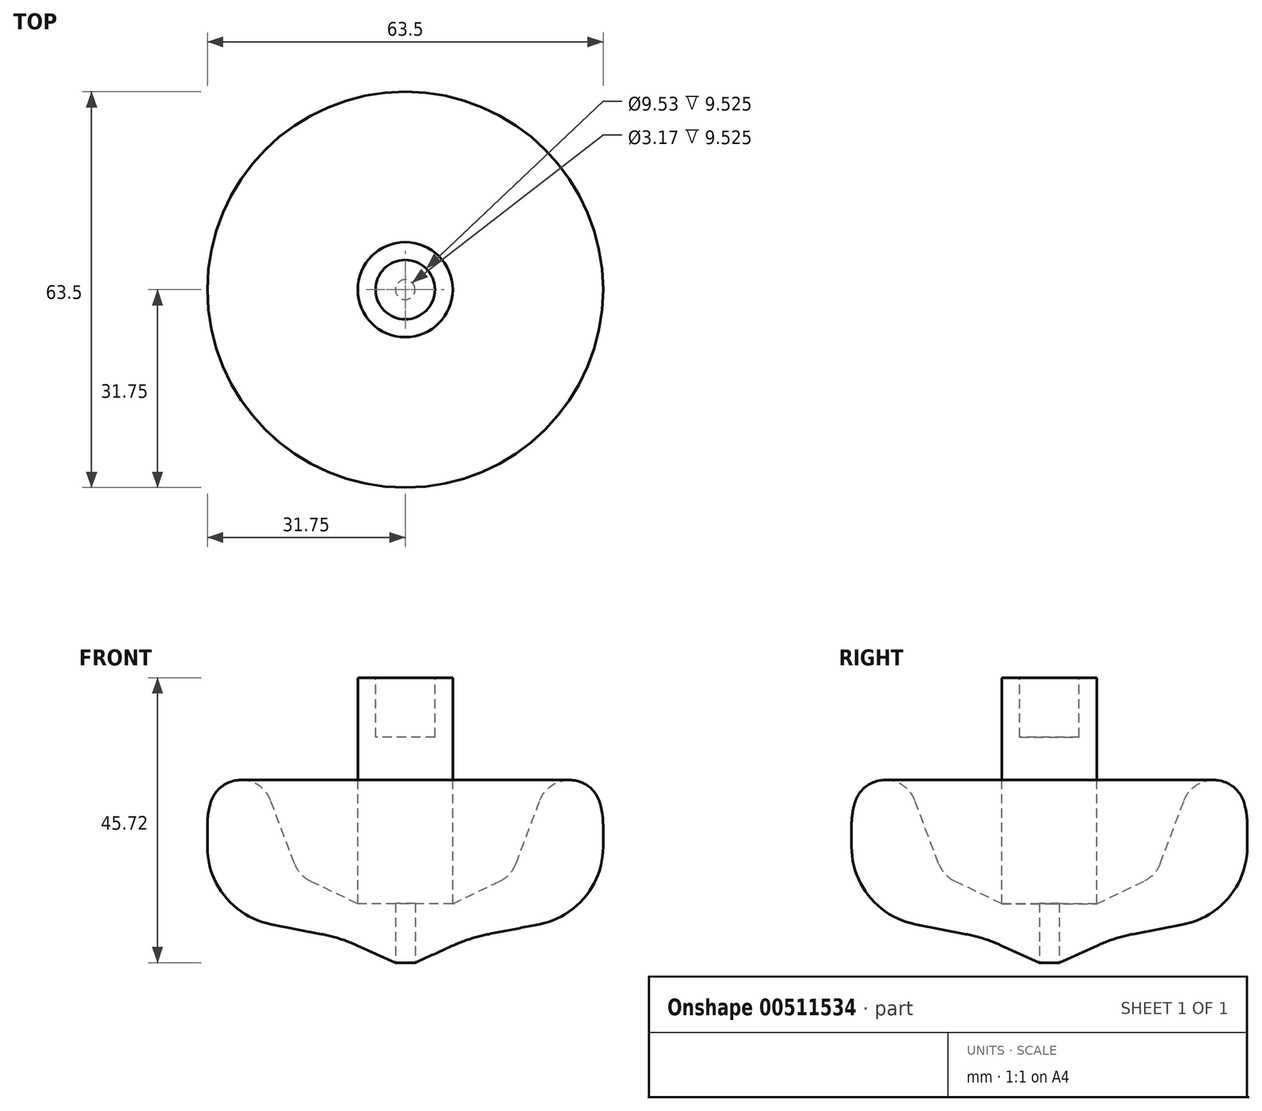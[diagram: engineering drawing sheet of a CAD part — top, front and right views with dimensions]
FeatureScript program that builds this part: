
annotation { "Feature Type Name" : "Feature", "Feature Type Description" : "" }
export const myFeature = defineFeature(function(context is Context, id is Id, definition is map)
    precondition{}
    {
        {
            var Q0;
            Q0=qCreatedBy(makeId("Front.planeOp"),FACE);
            var sketch = newSketch(context, id + "F0", { "sketchPlane" : qUnion([Q0])});
            skLineSegment(sketch, "E0", {"start": v(31.75, 8.13) * mm, "end": v(31.75, 33.53) * mm});
            skLineSegment(sketch, "E1", {"start": v(31.75, 33.53) * mm, "end": v(24.44, 33.53) * mm});
            skLineSegment(sketch, "E2", {"start": v(7.62, 9.44) * mm, "end": v(7.62, 45.72) * mm});
            skLineSegment(sketch, "E3", {"start": v(7.62, 45.72) * mm, "end": v(0, 45.72) * mm});
            skLineSegment(sketch, "E4", {"start": v(0, 45.72) * mm, "end": v(0, 0) * mm});
            skLineSegment(sketch, "E5", {"start": v(10.5, 4.02) * mm, "end": v(31.75, 8.13) * mm});
            skLineSegment(sketch, "E6", {"start": v(0, 0) * mm, "end": v(1.59, 0) * mm});
            skLineSegment(sketch, "E7", {"start": v(1.59, 0) * mm, "end": v(10.5, 4.02) * mm});
            skLineSegment(sketch, "E8", {"start": v(7.62, 9.44) * mm, "end": v(17.05, 13.98) * mm});
            skLineSegment(sketch, "E9", {"start": v(17.05, 13.98) * mm, "end": v(24.44, 33.53) * mm});
            skSolve(sketch);
        }
        {
            var Q0;
            Q0=qSketchRegion(id+"F0",true);
            var Q1;
            Q1=sQuery(id+"F0.wireOp",EDGE,"E4");
            revolve(context, id + "F1", {"entities" : qUnion([Q0]), "axis" : qUnion([Q1]), "revolveType" : RevolveType.FULL});
        }
        {
            var Q0;
            Q0=makeQuery(id+"F1.opRevolve","SWEPT_EDGE",EDGE,{"disambiguationData":[OSD([sQuery(id+"F0.wireOp",EDGE,"E5"),sQuery(id+"F0.wireOp",EDGE,"E7")])]});
            fillet(context, id + "F2", {"entities" : qUnion([Q0]), "radius" : 25.4 * mm, "tangentPropagation" : true, "allowEdgeOverflow" : false});
        }
        {
            var Q0;
            Q0=makeQuery(id+"F1.opRevolve","SWEPT_FACE",FACE,{"disambiguationData":[OSD([sQuery(id+"F0.wireOp",EDGE,"E3")])]});
            var sketch = newSketch(context, id + "F3", { "sketchPlane" : qUnion([Q0])});
            skCircle(sketch, "E10", {"center": v(0, 0) * mm, "radius": 4.76 * mm});
            skSolve(sketch);
        }
        {
            var Q0;
            Q0=qSketchRegion(id+"F3",true);
            extrude(context, id + "F4", {"entities" : qUnion([Q0]), "operationType" : NewBodyOperationType.REMOVE, "oppositeDirection" : true, "depth" : 9.52 * mm});
        }
        {
            var Q0;
            Q0=qCreatedBy(makeId("Top.planeOp"),FACE);
            var sketch = newSketch(context, id + "F5", { "sketchPlane" : qUnion([Q0])});
            skCircle(sketch, "E11", {"center": v(0, 0) * mm, "radius": 1.59 * mm});
            skSolve(sketch);
        }
        {
            var Q0;
            Q0=qSketchRegion(id+"F5",true);
            extrude(context, id + "F6", {"entities" : qUnion([Q0]), "operationType" : NewBodyOperationType.REMOVE, "depth" : 9.52 * mm});
        }
        {
            var Q0;
            Q0=makeQuery(id+"F1.opRevolve","SWEPT_FACE",FACE,{"disambiguationData":[OSD([sQuery(id+"F0.wireOp",EDGE,"E0")])]});
            fillet(context, id + "F7", {"entities" : qUnion([Q0]), "radius" : 12.7 * mm, "tangentPropagation" : true, "allowEdgeOverflow" : false});
        }
        {
            var Q0;
            Q0=makeQuery(id+"F1.opRevolve","SWEPT_FACE",FACE,{"disambiguationData":[OSD([sQuery(id+"F0.wireOp",EDGE,"E9")])]});
            fillet(context, id + "F8", {"entities" : qUnion([Q0]), "radius" : 5.08 * mm, "tangentPropagation" : true, "allowEdgeOverflow" : false});
        }
    });
